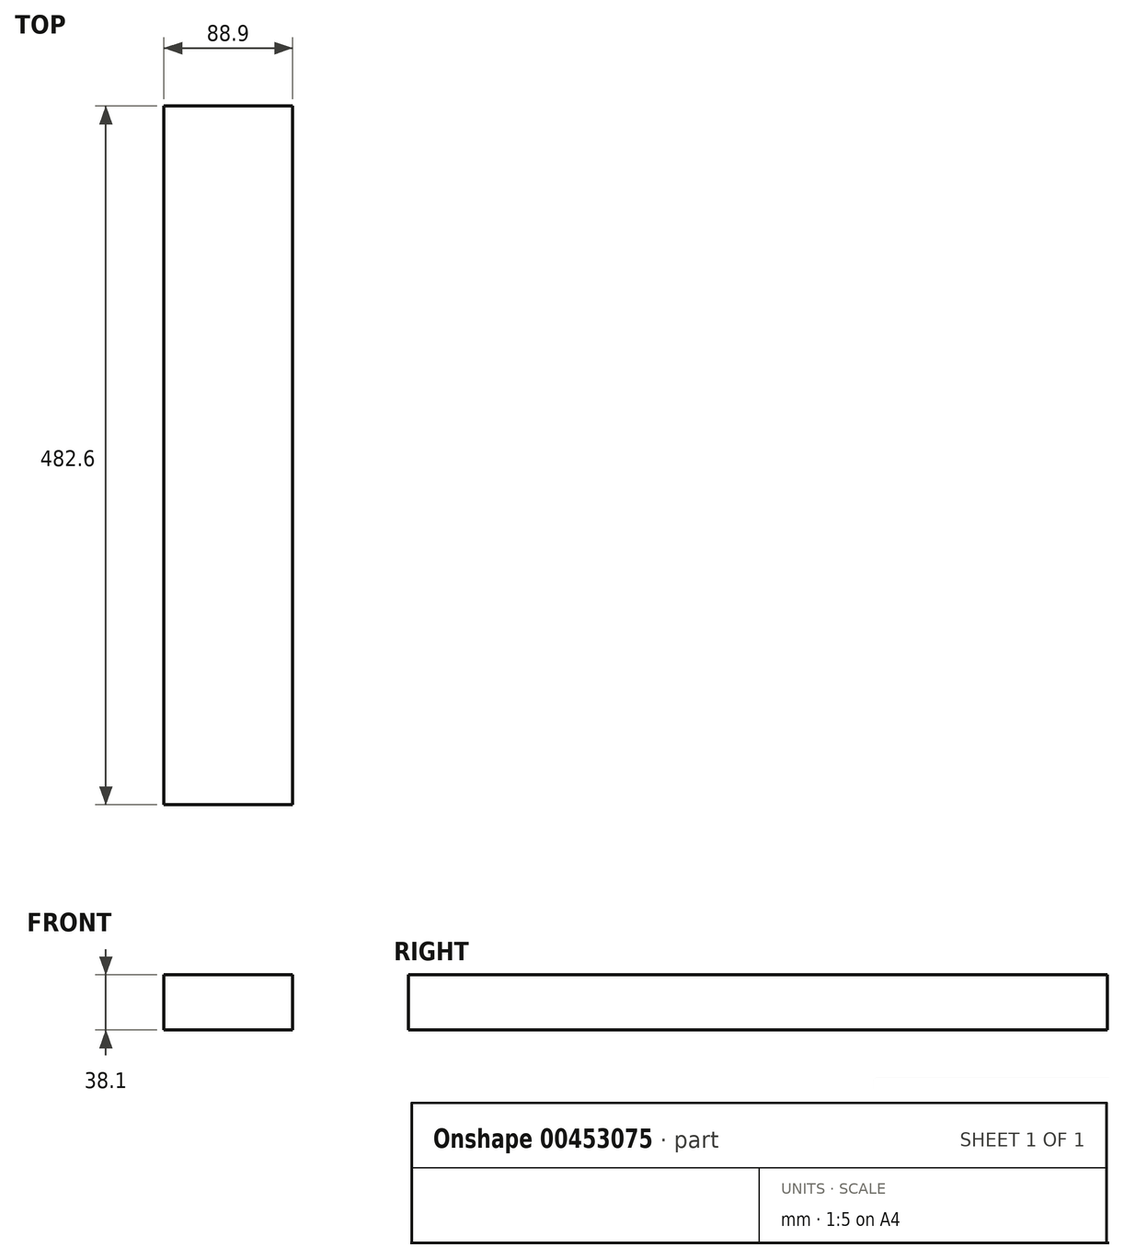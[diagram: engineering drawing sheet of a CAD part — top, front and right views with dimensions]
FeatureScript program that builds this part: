
annotation { "Feature Type Name" : "Feature", "Feature Type Description" : "" }
export const myFeature = defineFeature(function(context is Context, id is Id, definition is map)
    precondition{}
    {
        {
            var Q0;
            Q0=qCreatedBy(makeId("Front.planeOp"),FACE);
            var sketch = newSketch(context, id + "F0", { "sketchPlane" : qUnion([Q0])});
            skLineSegment(sketch, "E0.bottom", {"start": v(44.45, 19.05) * mm, "end": v(-44.45, 19.05) * mm});
            skLineSegment(sketch, "E0.top", {"start": v(44.45, -19.05) * mm, "end": v(-44.45, -19.05) * mm});
            skLineSegment(sketch, "E0.left", {"start": v(44.45, 19.05) * mm, "end": v(44.45, -19.05) * mm});
            skLineSegment(sketch, "E0.right", {"start": v(-44.45, 19.05) * mm, "end": v(-44.45, -19.05) * mm});
            skPoint(sketch, "E0.middle", {"position": v(0, 0) * mm});
            skSolve(sketch);
        }
        {
            var Q0;
            Q0 = qSketchRegion(id + "F0", true);
            extrude(context, id + "F1", {"entities" : qUnion([Q0]), "depth" : 482.6 * mm, "offsetDistance" : 25.4 * mm});
        }
    });
